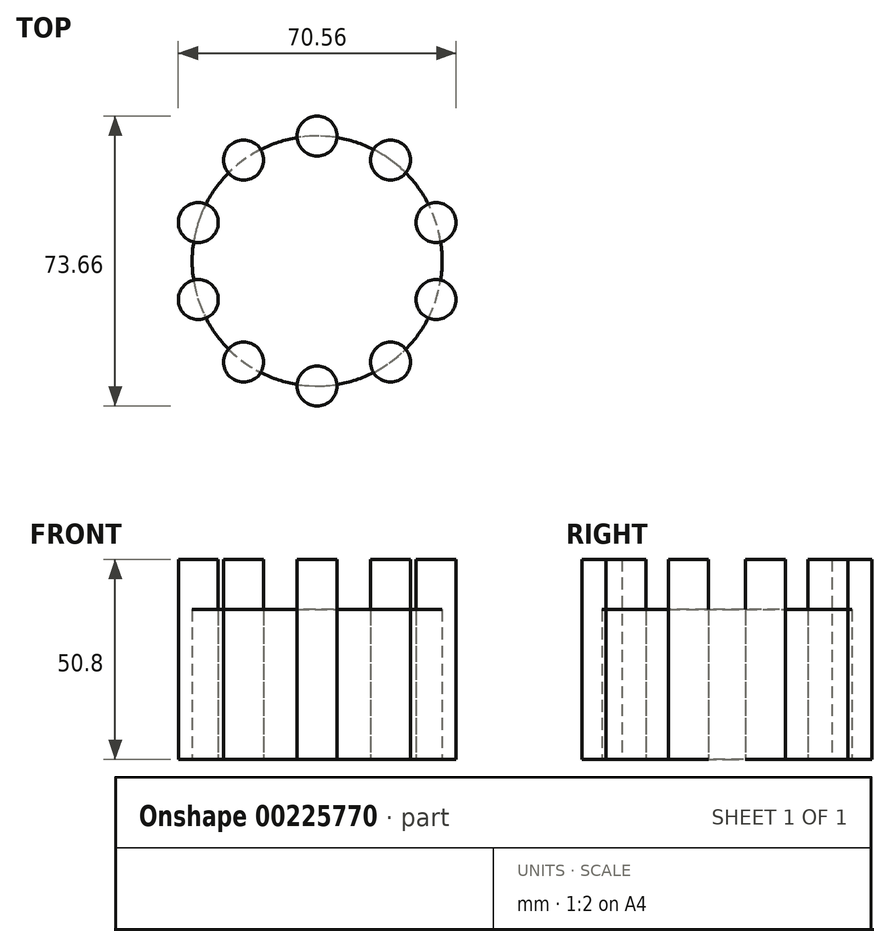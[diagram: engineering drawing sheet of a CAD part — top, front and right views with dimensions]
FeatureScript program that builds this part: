
annotation { "Feature Type Name" : "Feature", "Feature Type Description" : "" }
export const myFeature = defineFeature(function(context is Context, id is Id, definition is map)
    precondition{}
    {
        {
            var Q0;
            Q0=qCreatedBy(makeId("Top.planeOp"),FACE);
            var sketch = newSketch(context, id + "F0", { "sketchPlane" : qUnion([Q0])});
            skCircle(sketch, "E0", {"center": v(0, 0) * mm, "radius": 31.75 * mm});
            skSolve(sketch);
        }
        {
            var Q0;
            Q0=qSketchRegion(id+"F0",true);
            extrude(context, id + "F1", {"entities" : qUnion([Q0]), "depth" : 38.1 * mm});
        }
        {
            var Q0;
            Q0=qCreatedBy(makeId("Top.planeOp"),FACE);
            var sketch = newSketch(context, id + "F2", { "sketchPlane" : qUnion([Q0])});
            skCircle(sketch, "E1", {"center": v(0, 31.75) * mm, "radius": 5.08 * mm});
            skCircle(sketch, "E2.1.0", {"center": v(-18.66, 25.69) * mm, "radius": 5.08 * mm});
            skCircle(sketch, "E2.2.0", {"center": v(-30.2, 9.81) * mm, "radius": 5.08 * mm});
            skCircle(sketch, "E2.3.0", {"center": v(-30.2, -9.81) * mm, "radius": 5.08 * mm});
            skCircle(sketch, "E2.4.0", {"center": v(-18.66, -25.69) * mm, "radius": 5.08 * mm});
            skCircle(sketch, "E2.5.0", {"center": v(0, -31.75) * mm, "radius": 5.08 * mm});
            skCircle(sketch, "E2.6.0", {"center": v(18.66, -25.69) * mm, "radius": 5.08 * mm});
            skCircle(sketch, "E2.7.0", {"center": v(30.2, -9.81) * mm, "radius": 5.08 * mm});
            skCircle(sketch, "E2.8.0", {"center": v(30.2, 9.81) * mm, "radius": 5.08 * mm});
            skCircle(sketch, "E2.9.0", {"center": v(18.66, 25.69) * mm, "radius": 5.08 * mm});
            skPoint(sketch, "E2.center", {"position": v(0, 0) * mm});
            skSolve(sketch);
        }
        {
            var Q0;
            Q0=qSketchRegion(id+"F2",true);
            extrude(context, id + "F3", {"entities" : qUnion([Q0]), "depth" : 50.8 * mm});
        }
    });
